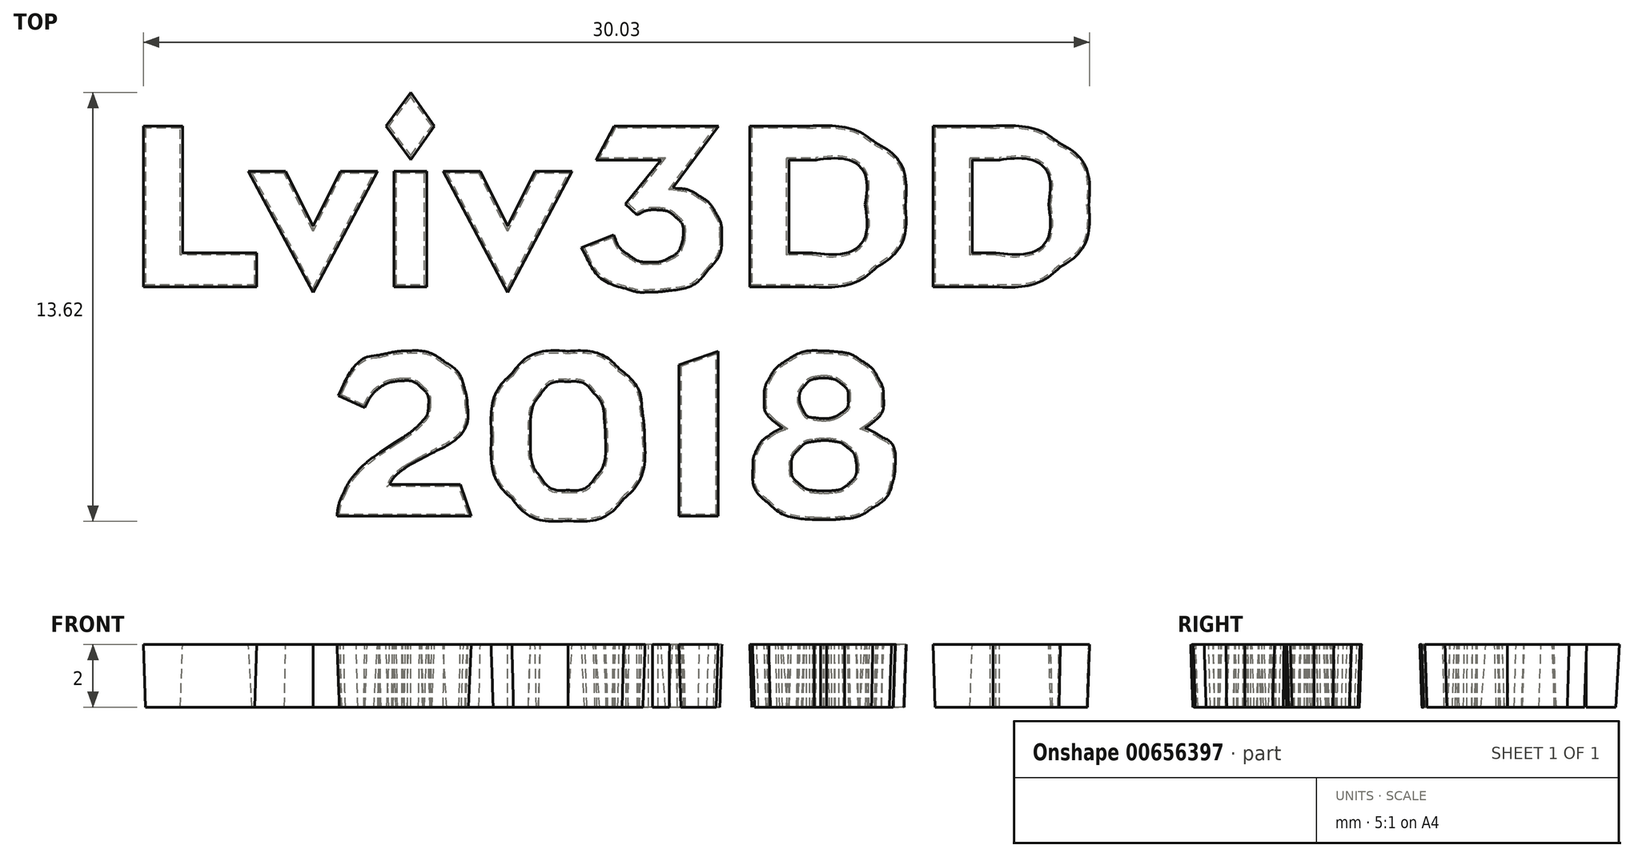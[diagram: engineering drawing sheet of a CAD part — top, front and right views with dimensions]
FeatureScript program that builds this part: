
annotation { "Feature Type Name" : "Feature", "Feature Type Description" : "" }
export const myFeature = defineFeature(function(context is Context, id is Id, definition is map)
    precondition{}
    {
        {
            var Q0;
            Q0=qCreatedBy(makeId("Top.planeOp"),FACE);
            var sketch = newSketch(context, id + "F0", { "sketchPlane" : qUnion([Q0])});
            skLineSegment(sketch, "E0", {"start": v(11.3, 1.71) * mm, "end": v(12.05, 1.71) * mm});
            skLineSegment(sketch, "E1", {"start": v(12.17, 4.66) * mm, "end": v(11.3, 4.66) * mm});
            skLineSegment(sketch, "E2", {"start": v(11.3, 4.66) * mm, "end": v(11.3, 1.71) * mm});
            skLineSegment(sketch, "E3", {"start": v(10.06, 0.63) * mm, "end": v(10.06, 5.73) * mm});
            skLineSegment(sketch, "E4", {"start": v(10.06, 5.73) * mm, "end": v(11.87, 5.73) * mm});
            skLineSegment(sketch, "E5", {"start": v(11.96, 0.63) * mm, "end": v(10.06, 0.63) * mm});
            skLineSegment(sketch, "E6", {"start": v(5.48, 1.71) * mm, "end": v(6.23, 1.71) * mm});
            skLineSegment(sketch, "E7", {"start": v(6.35, 4.66) * mm, "end": v(5.48, 4.66) * mm});
            skLineSegment(sketch, "E8", {"start": v(5.48, 4.66) * mm, "end": v(5.48, 1.71) * mm});
            skLineSegment(sketch, "E9", {"start": v(4.24, 0.63) * mm, "end": v(4.24, 5.73) * mm});
            skLineSegment(sketch, "E10", {"start": v(4.24, 5.73) * mm, "end": v(6.05, 5.73) * mm});
            skLineSegment(sketch, "E11", {"start": v(6.14, 0.63) * mm, "end": v(4.24, 0.63) * mm});
            skLineSegment(sketch, "E12", {"start": v(-1.1, 1.87) * mm, "end": v(-0.08, 2.28) * mm});
            skLineSegment(sketch, "E13", {"start": v(-0.08, 2.28) * mm, "end": v(-0.02, 2.13) * mm});
            skLineSegment(sketch, "E14", {"start": v(1.03, 1.42) * mm, "end": v(1.14, 1.42) * mm});
            skLineSegment(sketch, "E15", {"start": v(2.07, 1.97) * mm, "end": v(2.12, 2.13) * mm});
            skLineSegment(sketch, "E16", {"start": v(0.75, 2.96) * mm, "end": v(0.66, 2.92) * mm});
            skLineSegment(sketch, "E17", {"start": v(0.66, 2.92) * mm, "end": v(0.3, 3.26) * mm});
            skLineSegment(sketch, "E18", {"start": v(0.3, 3.26) * mm, "end": v(1.42, 4.66) * mm});
            skLineSegment(sketch, "E19", {"start": v(1.42, 4.66) * mm, "end": v(-0.64, 4.66) * mm});
            skLineSegment(sketch, "E20", {"start": v(-0.64, 4.66) * mm, "end": v(-0.07, 5.74) * mm});
            skLineSegment(sketch, "E21", {"start": v(-0.07, 5.74) * mm, "end": v(3.26, 5.73) * mm});
            skLineSegment(sketch, "E22", {"start": v(3.26, 5.73) * mm, "end": v(1.8, 3.77) * mm});
            skLineSegment(sketch, "E23", {"start": v(1.8, 3.77) * mm, "end": v(1.95, 3.76) * mm});
            skLineSegment(sketch, "E24", {"start": v(-0.99, 1.68) * mm, "end": v(-1.1, 1.87) * mm});
            skLineSegment(sketch, "E25", {"start": v(-5.5, 4.3) * mm, "end": v(-4.3, 4.3) * mm});
            skLineSegment(sketch, "E26", {"start": v(-4.3, 4.3) * mm, "end": v(-3.44, 2.55) * mm});
            skLineSegment(sketch, "E27", {"start": v(-3.44, 2.55) * mm, "end": v(-2.57, 4.3) * mm});
            skLineSegment(sketch, "E28", {"start": v(-2.57, 4.3) * mm, "end": v(-1.4, 4.3) * mm});
            skLineSegment(sketch, "E29", {"start": v(-1.4, 4.3) * mm, "end": v(-3.44, 0.45) * mm});
            skLineSegment(sketch, "E30", {"start": v(-3.44, 0.45) * mm, "end": v(-5.5, 4.3) * mm});
            skLineSegment(sketch, "E31", {"start": v(-11.67, 4.3) * mm, "end": v(-10.48, 4.3) * mm});
            skLineSegment(sketch, "E32", {"start": v(-10.48, 4.3) * mm, "end": v(-9.62, 2.55) * mm});
            skLineSegment(sketch, "E33", {"start": v(-9.62, 2.55) * mm, "end": v(-8.75, 4.3) * mm});
            skLineSegment(sketch, "E34", {"start": v(-8.75, 4.3) * mm, "end": v(-7.57, 4.3) * mm});
            skLineSegment(sketch, "E35", {"start": v(-7.57, 4.3) * mm, "end": v(-9.62, 0.45) * mm});
            skLineSegment(sketch, "E36", {"start": v(-9.62, 0.45) * mm, "end": v(-11.67, 4.3) * mm});
            skLineSegment(sketch, "E37", {"start": v(-15, 0.63) * mm, "end": v(-15, 5.73) * mm});
            skLineSegment(sketch, "E38", {"start": v(-15, 5.73) * mm, "end": v(-13.75, 5.73) * mm});
            skLineSegment(sketch, "E39", {"start": v(-13.75, 5.73) * mm, "end": v(-13.75, 1.71) * mm});
            skLineSegment(sketch, "E40", {"start": v(-13.75, 1.71) * mm, "end": v(-11.4, 1.71) * mm});
            skLineSegment(sketch, "E41", {"start": v(-11.4, 1.71) * mm, "end": v(-11.4, 0.63) * mm});
            skLineSegment(sketch, "E42", {"start": v(-11.4, 0.63) * mm, "end": v(-15, 0.63) * mm});
            skLineSegment(sketch, "E43", {"start": v(-7.05, 0.63) * mm, "end": v(-7.05, 4.3) * mm});
            skLineSegment(sketch, "E44", {"start": v(-7.05, 4.3) * mm, "end": v(-6, 4.3) * mm});
            skLineSegment(sketch, "E45", {"start": v(-6, 4.3) * mm, "end": v(-6, 0.63) * mm});
            skLineSegment(sketch, "E46", {"start": v(-6, 0.63) * mm, "end": v(-7.05, 0.63) * mm});
            skLineSegment(sketch, "E47", {"start": v(-7.3, 5.73) * mm, "end": v(-6.52, 6.8) * mm});
            skLineSegment(sketch, "E48", {"start": v(-6.52, 6.8) * mm, "end": v(-5.76, 5.73) * mm});
            skLineSegment(sketch, "E49", {"start": v(-5.76, 5.73) * mm, "end": v(-6.52, 4.67) * mm});
            skLineSegment(sketch, "E50", {"start": v(-6.52, 4.67) * mm, "end": v(-7.3, 5.73) * mm});
            skLineSegment(sketch, "E51", {"start": v(-7.53, -4.66) * mm, "end": v(-7.5, -4.64) * mm});
            skLineSegment(sketch, "E52", {"start": v(-7.5, -4.64) * mm, "end": v(-6.97, -4.29) * mm});
            skLineSegment(sketch, "E53", {"start": v(-6.97, -4.29) * mm, "end": v(-6.77, -4.16) * mm});
            skLineSegment(sketch, "E54", {"start": v(-7.9, -3.05) * mm, "end": v(-7.97, -3.2) * mm});
            skLineSegment(sketch, "E55", {"start": v(-7.97, -3.2) * mm, "end": v(-8.81, -2.82) * mm});
            skLineSegment(sketch, "E56", {"start": v(-8.81, -2.82) * mm, "end": v(-8.71, -2.6) * mm});
            skLineSegment(sketch, "E57", {"start": v(-5.85, -4.65) * mm, "end": v(-6.23, -4.86) * mm});
            skLineSegment(sketch, "E58", {"start": v(-6.23, -4.86) * mm, "end": v(-6.5, -5) * mm});
            skLineSegment(sketch, "E59", {"start": v(-6.5, -5) * mm, "end": v(-6.59, -5.05) * mm});
            skLineSegment(sketch, "E60", {"start": v(-6.59, -5.05) * mm, "end": v(-6.68, -5.12) * mm});
            skLineSegment(sketch, "E61", {"start": v(-7.18, -5.64) * mm, "end": v(-4.94, -5.64) * mm});
            skLineSegment(sketch, "E62", {"start": v(-4.94, -5.64) * mm, "end": v(-4.6, -6.65) * mm});
            skLineSegment(sketch, "E63", {"start": v(-4.6, -6.65) * mm, "end": v(-8.86, -6.65) * mm});
            skLineSegment(sketch, "E64", {"start": v(2, -6.65) * mm, "end": v(2, -1.85) * mm});
            skLineSegment(sketch, "E65", {"start": v(2, -1.85) * mm, "end": v(3.24, -1.41) * mm});
            skLineSegment(sketch, "E66", {"start": v(3.24, -1.41) * mm, "end": v(3.24, -6.65) * mm});
            skLineSegment(sketch, "E67", {"start": v(3.24, -6.65) * mm, "end": v(2, -6.65) * mm});
            skLineSegment(sketch, "E68", {"start": v(5.28, -3.86) * mm, "end": v(5.24, -3.83) * mm});
            skLineSegment(sketch, "E69", {"start": v(5.24, -3.83) * mm, "end": v(5.15, -3.76) * mm});
            skLineSegment(sketch, "E70", {"start": v(5.15, -3.76) * mm, "end": v(5.02, -3.65) * mm});
            skLineSegment(sketch, "E71", {"start": v(8.18, -3.65) * mm, "end": v(8.05, -3.76) * mm});
            skLineSegment(sketch, "E72", {"start": v(8.05, -3.76) * mm, "end": v(7.96, -3.83) * mm});
            skLineSegment(sketch, "E73", {"start": v(7.96, -3.83) * mm, "end": v(7.9, -3.86) * mm});
            skFitSpline(sketch, "E74", {"points": [v(12.05, 1.71) * mm, v(13.17, 1.71) * mm, v(13.73, 2.22) * mm, v(13.73, 3.25) * mm]});
            skFitSpline(sketch, "E75", {"points": [v(13.73, 3.25) * mm, v(13.73, 4.19) * mm, v(13.2, 4.66) * mm, v(12.17, 4.66) * mm]});
            skFitSpline(sketch, "E76", {"points": [v(11.87, 5.73) * mm, v(12.8, 5.73) * mm, v(13.53, 5.56) * mm, v(14.06, 5.2) * mm]});
            skFitSpline(sketch, "E77", {"points": [v(14.06, 5.2) * mm, v(14.69, 4.77) * mm, v(15, 4.12) * mm, v(15, 3.23) * mm]});
            skFitSpline(sketch, "E78", {"points": [v(15, 3.23) * mm, v(15, 2.37) * mm, v(14.7, 1.72) * mm, v(14.1, 1.26) * mm]});
            skFitSpline(sketch, "E79", {"points": [v(14.1, 1.26) * mm, v(13.56, 0.84) * mm, v(12.85, 0.63) * mm, v(11.96, 0.63) * mm]});
            skFitSpline(sketch, "E80", {"points": [v(6.23, 1.71) * mm, v(7.35, 1.71) * mm, v(7.9, 2.22) * mm, v(7.9, 3.25) * mm]});
            skFitSpline(sketch, "E81", {"points": [v(7.9, 3.25) * mm, v(7.9, 4.19) * mm, v(7.39, 4.66) * mm, v(6.35, 4.66) * mm]});
            skFitSpline(sketch, "E82", {"points": [v(6.05, 5.73) * mm, v(6.98, 5.73) * mm, v(7.7, 5.56) * mm, v(8.24, 5.2) * mm]});
            skFitSpline(sketch, "E83", {"points": [v(8.24, 5.2) * mm, v(8.87, 4.77) * mm, v(9.18, 4.12) * mm, v(9.18, 3.23) * mm]});
            skFitSpline(sketch, "E84", {"points": [v(9.18, 3.23) * mm, v(9.18, 2.37) * mm, v(8.88, 1.72) * mm, v(8.28, 1.26) * mm]});
            skFitSpline(sketch, "E85", {"points": [v(8.28, 1.26) * mm, v(7.74, 0.84) * mm, v(7.03, 0.63) * mm, v(6.14, 0.63) * mm]});
            skFitSpline(sketch, "E86", {"points": [v(-0.02, 2.13) * mm, v(0.07, 1.94) * mm, v(0.21, 1.77) * mm, v(0.42, 1.63) * mm]});
            skFitSpline(sketch, "E87", {"points": [v(0.42, 1.63) * mm, v(0.62, 1.5) * mm, v(0.83, 1.42) * mm, v(1.03, 1.42) * mm]});
            skFitSpline(sketch, "E88", {"points": [v(1.14, 1.42) * mm, v(1.34, 1.42) * mm, v(1.53, 1.47) * mm, v(1.7, 1.55) * mm]});
            skFitSpline(sketch, "E89", {"points": [v(1.7, 1.55) * mm, v(1.88, 1.65) * mm, v(2, 1.8) * mm, v(2.07, 1.97) * mm]});
            skFitSpline(sketch, "E90", {"points": [v(2.12, 2.13) * mm, v(2.13, 2.2) * mm, v(2.13, 2.25) * mm, v(2.13, 2.28) * mm]});
            skFitSpline(sketch, "E91", {"points": [v(2.13, 2.28) * mm, v(2.13, 2.51) * mm, v(2.06, 2.7) * mm, v(1.9, 2.83) * mm]});
            skFitSpline(sketch, "E92", {"points": [v(1.9, 2.83) * mm, v(1.75, 2.97) * mm, v(1.56, 3.05) * mm, v(1.33, 3.07) * mm]});
            skFitSpline(sketch, "E93", {"points": [v(1.33, 3.07) * mm, v(1.1, 3.07) * mm, v(0.9, 3.03) * mm, v(0.75, 2.96) * mm]});
            skFitSpline(sketch, "E94", {"points": [v(1.95, 3.76) * mm, v(2.2, 3.73) * mm, v(2.43, 3.65) * mm, v(2.65, 3.51) * mm]});
            skFitSpline(sketch, "E95", {"points": [v(2.65, 3.51) * mm, v(2.87, 3.37) * mm, v(3.04, 3.2) * mm, v(3.16, 2.99) * mm]});
            skFitSpline(sketch, "E96", {"points": [v(3.16, 2.99) * mm, v(3.29, 2.76) * mm, v(3.35, 2.51) * mm, v(3.35, 2.25) * mm]});
            skFitSpline(sketch, "E97", {"points": [v(3.35, 2.25) * mm, v(3.35, 1.87) * mm, v(3.21, 1.51) * mm, v(2.94, 1.19) * mm]});
            skFitSpline(sketch, "E98", {"points": [v(2.94, 1.19) * mm, v(2.63, 0.81) * mm, v(2.21, 0.59) * mm, v(1.7, 0.51) * mm]});
            skFitSpline(sketch, "E99", {"points": [v(1.7, 0.51) * mm, v(1.47, 0.48) * mm, v(1.3, 0.47) * mm, v(1.16, 0.47) * mm]});
            skFitSpline(sketch, "E100", {"points": [v(1.16, 0.47) * mm, v(0.97, 0.47) * mm, v(0.73, 0.46) * mm, v(0.3, 0.58) * mm]});
            skFitSpline(sketch, "E101", {"points": [v(0.3, 0.58) * mm, v(-0.13, 0.7) * mm, v(-0.61, 1.02) * mm, v(-0.99, 1.68) * mm]});
            skFitSpline(sketch, "E102", {"points": [v(-8.86, -6.65) * mm, v(-8.83, -6.4) * mm, v(-8.76, -6.16) * mm, v(-8.65, -5.92) * mm]});
            skFitSpline(sketch, "E103", {"points": [v(-8.65, -5.92) * mm, v(-8.54, -5.67) * mm, v(-8.4, -5.46) * mm, v(-8.25, -5.27) * mm]});
            skFitSpline(sketch, "E104", {"points": [v(-8.25, -5.27) * mm, v(-8.08, -5.08) * mm, v(-7.84, -4.88) * mm, v(-7.53, -4.66) * mm]});
            skFitSpline(sketch, "E105", {"points": [v(-6.77, -4.16) * mm, v(-6.48, -3.96) * mm, v(-6.28, -3.79) * mm, v(-6.16, -3.65) * mm]});
            skFitSpline(sketch, "E106", {"points": [v(-6.16, -3.65) * mm, v(-6.05, -3.51) * mm, v(-5.98, -3.4) * mm, v(-5.97, -3.32) * mm]});
            skFitSpline(sketch, "E107", {"points": [v(-5.97, -3.32) * mm, v(-5.96, -3.24) * mm, v(-5.95, -3.18) * mm, v(-5.95, -3.13) * mm]});
            skFitSpline(sketch, "E108", {"points": [v(-5.95, -3.13) * mm, v(-5.95, -2.9) * mm, v(-6.03, -2.72) * mm, v(-6.18, -2.57) * mm]});
            skFitSpline(sketch, "E109", {"points": [v(-6.18, -2.57) * mm, v(-6.34, -2.43) * mm, v(-6.54, -2.35) * mm, v(-6.8, -2.35) * mm]});
            skFitSpline(sketch, "E110", {"points": [v(-6.8, -2.35) * mm, v(-6.86, -2.35) * mm, v(-6.96, -2.37) * mm, v(-7.1, -2.39) * mm]});
            skFitSpline(sketch, "E111", {"points": [v(-7.1, -2.39) * mm, v(-7.24, -2.41) * mm, v(-7.37, -2.48) * mm, v(-7.52, -2.59) * mm]});
            skFitSpline(sketch, "E112", {"points": [v(-7.52, -2.59) * mm, v(-7.66, -2.7) * mm, v(-7.79, -2.85) * mm, v(-7.9, -3.05) * mm]});
            skFitSpline(sketch, "E113", {"points": [v(-8.71, -2.6) * mm, v(-8.37, -1.99) * mm, v(-7.98, -1.63) * mm, v(-7.53, -1.54) * mm]});
            skFitSpline(sketch, "E114", {"points": [v(-7.53, -1.54) * mm, v(-7.08, -1.45) * mm, v(-6.77, -1.4) * mm, v(-6.6, -1.4) * mm]});
            skFitSpline(sketch, "E115", {"points": [v(-6.6, -1.4) * mm, v(-6.17, -1.4) * mm, v(-5.78, -1.52) * mm, v(-5.45, -1.75) * mm]});
            skFitSpline(sketch, "E116", {"points": [v(-5.45, -1.75) * mm, v(-5.12, -1.97) * mm, v(-4.91, -2.22) * mm, v(-4.84, -2.49) * mm]});
            skFitSpline(sketch, "E117", {"points": [v(-4.84, -2.49) * mm, v(-4.76, -2.76) * mm, v(-4.73, -2.96) * mm, v(-4.73, -3.1) * mm]});
            skFitSpline(sketch, "E118", {"points": [v(-4.73, -3.1) * mm, v(-4.73, -3.71) * mm, v(-5.1, -4.23) * mm, v(-5.85, -4.65) * mm]});
            skFitSpline(sketch, "E119", {"points": [v(-6.68, -5.12) * mm, v(-6.84, -5.23) * mm, v(-6.95, -5.32) * mm, v(-7.02, -5.4) * mm]});
            skFitSpline(sketch, "E120", {"points": [v(-7.02, -5.4) * mm, v(-7.09, -5.46) * mm, v(-7.14, -5.55) * mm, v(-7.18, -5.64) * mm]});
            skFitSpline(sketch, "E121", {"points": [v(-3.95, -4.1) * mm, v(-3.95, -3.25) * mm, v(-3.74, -2.6) * mm, v(-3.3, -2.12) * mm]});
            skFitSpline(sketch, "E122", {"points": [v(-3.3, -2.12) * mm, v(-2.87, -1.65) * mm, v(-2.28, -1.41) * mm, v(-1.53, -1.41) * mm]});
            skFitSpline(sketch, "E123", {"points": [v(-1.53, -1.41) * mm, v(-0.86, -1.41) * mm, v(-0.32, -1.6) * mm, v(0.1, -1.97) * mm]});
            skFitSpline(sketch, "E124", {"points": [v(0.1, -1.97) * mm, v(0.52, -2.34) * mm, v(0.76, -2.75) * mm, v(0.82, -3.2) * mm]});
            skFitSpline(sketch, "E125", {"points": [v(0.82, -3.2) * mm, v(0.87, -3.64) * mm, v(0.9, -3.96) * mm, v(0.9, -4.16) * mm]});
            skFitSpline(sketch, "E126", {"points": [v(0.9, -4.16) * mm, v(0.9, -4.99) * mm, v(0.68, -5.63) * mm, v(0.24, -6.1) * mm]});
            skFitSpline(sketch, "E127", {"points": [v(0.24, -6.1) * mm, v(-0.2, -6.56) * mm, v(-0.78, -6.8) * mm, v(-1.53, -6.8) * mm]});
            skFitSpline(sketch, "E128", {"points": [v(-1.53, -6.8) * mm, v(-2.28, -6.8) * mm, v(-2.88, -6.56) * mm, v(-3.3, -6.1) * mm]});
            skFitSpline(sketch, "E129", {"points": [v(-3.3, -6.1) * mm, v(-3.74, -5.63) * mm, v(-3.95, -4.96) * mm, v(-3.95, -4.1) * mm]});
            skFitSpline(sketch, "E130", {"points": [v(-2.71, -4.1) * mm, v(-2.71, -4.68) * mm, v(-2.6, -5.11) * mm, v(-2.4, -5.4) * mm]});
            skFitSpline(sketch, "E131", {"points": [v(-2.4, -5.4) * mm, v(-2.2, -5.68) * mm, v(-1.9, -5.83) * mm, v(-1.53, -5.83) * mm]});
            skFitSpline(sketch, "E132", {"points": [v(-1.53, -5.83) * mm, v(-1.16, -5.83) * mm, v(-0.87, -5.69) * mm, v(-0.66, -5.41) * mm]});
            skFitSpline(sketch, "E133", {"points": [v(-0.66, -5.41) * mm, v(-0.44, -5.14) * mm, v(-0.34, -4.72) * mm, v(-0.34, -4.16) * mm]});
            skFitSpline(sketch, "E134", {"points": [v(-0.34, -4.16) * mm, v(-0.34, -4.03) * mm, v(-0.35, -3.82) * mm, v(-0.38, -3.52) * mm]});
            skFitSpline(sketch, "E135", {"points": [v(-0.38, -3.52) * mm, v(-0.4, -3.22) * mm, v(-0.52, -2.96) * mm, v(-0.72, -2.73) * mm]});
            skFitSpline(sketch, "E136", {"points": [v(-0.72, -2.73) * mm, v(-0.92, -2.5) * mm, v(-1.19, -2.38) * mm, v(-1.53, -2.38) * mm]});
            skFitSpline(sketch, "E137", {"points": [v(-1.53, -2.38) * mm, v(-1.9, -2.38) * mm, v(-2.2, -2.52) * mm, v(-2.4, -2.8) * mm]});
            skFitSpline(sketch, "E138", {"points": [v(-2.4, -2.8) * mm, v(-2.6, -3.1) * mm, v(-2.71, -3.52) * mm, v(-2.71, -4.1) * mm]});
            skFitSpline(sketch, "E139", {"points": [v(4.34, -5.15) * mm, v(4.34, -4.92) * mm, v(4.38, -4.72) * mm, v(4.46, -4.54) * mm]});
            skFitSpline(sketch, "E140", {"points": [v(4.46, -4.54) * mm, v(4.55, -4.37) * mm, v(4.66, -4.23) * mm, v(4.79, -4.14) * mm]});
            skFitSpline(sketch, "E141", {"points": [v(4.79, -4.14) * mm, v(4.92, -4.04) * mm, v(5.02, -3.98) * mm, v(5.07, -3.95) * mm]});
            skFitSpline(sketch, "E142", {"points": [v(5.07, -3.95) * mm, v(5.13, -3.92) * mm, v(5.2, -3.88) * mm, v(5.28, -3.86) * mm]});
            skFitSpline(sketch, "E143", {"points": [v(5.02, -3.65) * mm, v(4.8, -3.46) * mm, v(4.7, -3.2) * mm, v(4.7, -2.9) * mm]});
            skFitSpline(sketch, "E144", {"points": [v(4.7, -2.9) * mm, v(4.7, -2.68) * mm, v(4.76, -2.47) * mm, v(4.87, -2.27) * mm]});
            skFitSpline(sketch, "E145", {"points": [v(4.87, -2.27) * mm, v(4.98, -2.06) * mm, v(5.18, -1.87) * mm, v(5.45, -1.68) * mm]});
            skFitSpline(sketch, "E146", {"points": [v(5.45, -1.68) * mm, v(5.74, -1.5) * mm, v(6.12, -1.4) * mm, v(6.59, -1.4) * mm]});
            skFitSpline(sketch, "E147", {"points": [v(6.59, -1.4) * mm, v(6.7, -1.4) * mm, v(6.86, -1.42) * mm, v(7.08, -1.44) * mm]});
            skFitSpline(sketch, "E148", {"points": [v(7.08, -1.44) * mm, v(7.3, -1.46) * mm, v(7.54, -1.56) * mm, v(7.79, -1.72) * mm]});
            skFitSpline(sketch, "E149", {"points": [v(7.79, -1.72) * mm, v(8.03, -1.88) * mm, v(8.2, -2.06) * mm, v(8.32, -2.27) * mm]});
            skFitSpline(sketch, "E150", {"points": [v(8.32, -2.27) * mm, v(8.43, -2.48) * mm, v(8.49, -2.69) * mm, v(8.49, -2.9) * mm]});
            skFitSpline(sketch, "E151", {"points": [v(8.49, -2.9) * mm, v(8.49, -3.2) * mm, v(8.38, -3.46) * mm, v(8.18, -3.65) * mm]});
            skFitSpline(sketch, "E152", {"points": [v(7.9, -3.86) * mm, v(8.01, -3.9) * mm, v(8.2, -4) * mm, v(8.46, -4.15) * mm]});
            skFitSpline(sketch, "E153", {"points": [v(8.46, -4.15) * mm, v(8.72, -4.3) * mm, v(8.86, -4.62) * mm, v(8.86, -5.1) * mm]});
            skFitSpline(sketch, "E154", {"points": [v(8.86, -5.1) * mm, v(8.86, -5.24) * mm, v(8.82, -5.44) * mm, v(8.74, -5.7) * mm]});
            skFitSpline(sketch, "E155", {"points": [v(8.74, -5.7) * mm, v(8.67, -5.94) * mm, v(8.47, -6.17) * mm, v(8.15, -6.39) * mm]});
            skFitSpline(sketch, "E156", {"points": [v(8.15, -6.39) * mm, v(7.83, -6.6) * mm, v(7.53, -6.7) * mm, v(7.25, -6.73) * mm]});
            skFitSpline(sketch, "E157", {"points": [v(7.25, -6.73) * mm, v(6.98, -6.76) * mm, v(6.79, -6.77) * mm, v(6.69, -6.77) * mm]});
            skFitSpline(sketch, "E158", {"points": [v(6.69, -6.77) * mm, v(6.62, -6.77) * mm, v(6.56, -6.77) * mm, v(6.49, -6.76) * mm]});
            skFitSpline(sketch, "E159", {"points": [v(6.49, -6.76) * mm, v(6.42, -6.76) * mm, v(6.36, -6.76) * mm, v(6.3, -6.76) * mm]});
            skFitSpline(sketch, "E160", {"points": [v(6.3, -6.76) * mm, v(5.67, -6.7) * mm, v(5.19, -6.53) * mm, v(4.85, -6.24) * mm]});
            skFitSpline(sketch, "E161", {"points": [v(4.85, -6.24) * mm, v(4.51, -5.96) * mm, v(4.34, -5.6) * mm, v(4.34, -5.15) * mm]});
            skFitSpline(sketch, "E162", {"points": [v(5.82, -2.96) * mm, v(5.82, -3) * mm, v(5.83, -3.04) * mm, v(5.84, -3.08) * mm]});
            skFitSpline(sketch, "E163", {"points": [v(5.84, -3.08) * mm, v(5.86, -3.12) * mm, v(5.9, -3.2) * mm, v(5.96, -3.32) * mm]});
            skFitSpline(sketch, "E164", {"points": [v(5.96, -3.32) * mm, v(6.02, -3.44) * mm, v(6.13, -3.5) * mm, v(6.28, -3.52) * mm]});
            skFitSpline(sketch, "E165", {"points": [v(6.28, -3.52) * mm, v(6.43, -3.54) * mm, v(6.54, -3.55) * mm, v(6.59, -3.55) * mm]});
            skFitSpline(sketch, "E166", {"points": [v(6.59, -3.55) * mm, v(6.65, -3.55) * mm, v(6.7, -3.55) * mm, v(6.76, -3.54) * mm]});
            skFitSpline(sketch, "E167", {"points": [v(6.76, -3.54) * mm, v(6.82, -3.54) * mm, v(6.87, -3.52) * mm, v(6.94, -3.5) * mm]});
            skFitSpline(sketch, "E168", {"points": [v(6.94, -3.5) * mm, v(7, -3.47) * mm, v(7.08, -3.42) * mm, v(7.2, -3.34) * mm]});
            skFitSpline(sketch, "E169", {"points": [v(7.2, -3.34) * mm, v(7.31, -3.25) * mm, v(7.37, -3.11) * mm, v(7.37, -2.91) * mm]});
            skFitSpline(sketch, "E170", {"points": [v(7.37, -2.91) * mm, v(7.37, -2.73) * mm, v(7.3, -2.58) * mm, v(7.18, -2.47) * mm]});
            skFitSpline(sketch, "E171", {"points": [v(7.18, -2.47) * mm, v(7.05, -2.37) * mm, v(6.94, -2.3) * mm, v(6.84, -2.3) * mm]});
            skFitSpline(sketch, "E172", {"points": [v(6.84, -2.3) * mm, v(6.74, -2.27) * mm, v(6.66, -2.26) * mm, v(6.6, -2.26) * mm]});
            skFitSpline(sketch, "E173", {"points": [v(6.6, -2.26) * mm, v(6.53, -2.26) * mm, v(6.44, -2.27) * mm, v(6.33, -2.3) * mm]});
            skFitSpline(sketch, "E174", {"points": [v(6.33, -2.3) * mm, v(6.21, -2.3) * mm, v(6.1, -2.38) * mm, v(5.99, -2.51) * mm]});
            skFitSpline(sketch, "E175", {"points": [v(5.99, -2.51) * mm, v(5.88, -2.64) * mm, v(5.82, -2.79) * mm, v(5.82, -2.96) * mm]});
            skFitSpline(sketch, "E176", {"points": [v(5.57, -5.1) * mm, v(5.57, -5.3) * mm, v(5.64, -5.47) * mm, v(5.8, -5.6) * mm]});
            skFitSpline(sketch, "E177", {"points": [v(5.8, -5.6) * mm, v(5.95, -5.74) * mm, v(6.1, -5.81) * mm, v(6.26, -5.83) * mm]});
            skFitSpline(sketch, "E178", {"points": [v(6.26, -5.83) * mm, v(6.41, -5.85) * mm, v(6.52, -5.85) * mm, v(6.58, -5.85) * mm]});
            skFitSpline(sketch, "E179", {"points": [v(6.58, -5.85) * mm, v(6.66, -5.85) * mm, v(6.78, -5.85) * mm, v(6.94, -5.83) * mm]});
            skFitSpline(sketch, "E180", {"points": [v(6.94, -5.83) * mm, v(7.1, -5.81) * mm, v(7.24, -5.74) * mm, v(7.4, -5.6) * mm]});
            skFitSpline(sketch, "E181", {"points": [v(7.4, -5.6) * mm, v(7.55, -5.46) * mm, v(7.63, -5.28) * mm, v(7.63, -5.07) * mm]});
            skFitSpline(sketch, "E182", {"points": [v(7.63, -5.07) * mm, v(7.63, -5.04) * mm, v(7.63, -5.02) * mm, v(7.63, -4.99) * mm]});
            skFitSpline(sketch, "E183", {"points": [v(7.63, -4.99) * mm, v(7.62, -4.95) * mm, v(7.62, -4.92) * mm, v(7.62, -4.9) * mm]});
            skFitSpline(sketch, "E184", {"points": [v(7.62, -4.9) * mm, v(7.58, -4.73) * mm, v(7.49, -4.59) * mm, v(7.35, -4.48) * mm]});
            skFitSpline(sketch, "E185", {"points": [v(7.35, -4.48) * mm, v(7.2, -4.37) * mm, v(7.07, -4.3) * mm, v(6.94, -4.28) * mm]});
            skFitSpline(sketch, "E186", {"points": [v(6.94, -4.28) * mm, v(6.8, -4.26) * mm, v(6.71, -4.25) * mm, v(6.68, -4.25) * mm]});
            skFitSpline(sketch, "E187", {"points": [v(6.68, -4.25) * mm, v(6.65, -4.25) * mm, v(6.62, -4.25) * mm, v(6.6, -4.25) * mm]});
            skFitSpline(sketch, "E188", {"points": [v(6.6, -4.25) * mm, v(6.52, -4.25) * mm, v(6.4, -4.26) * mm, v(6.24, -4.29) * mm]});
            skFitSpline(sketch, "E189", {"points": [v(6.24, -4.29) * mm, v(6.08, -4.3) * mm, v(5.93, -4.4) * mm, v(5.78, -4.55) * mm]});
            skFitSpline(sketch, "E190", {"points": [v(5.78, -4.55) * mm, v(5.64, -4.7) * mm, v(5.57, -4.89) * mm, v(5.57, -5.1) * mm]});
            skSolve(sketch);
        }
        {
            var Q0;
            Q0 = qSketchRegion(id + "F0", true);
            extrude(context, id + "F1", {"entities" : qUnion([Q0]), "oppositeDirection" : true, "depth" : 2 * mm, "offsetDistance" : 25 * mm, "hasDraft" : true, "draftAngle" : 2 * degree, "draftPullDirection" : true});
        }
    });
